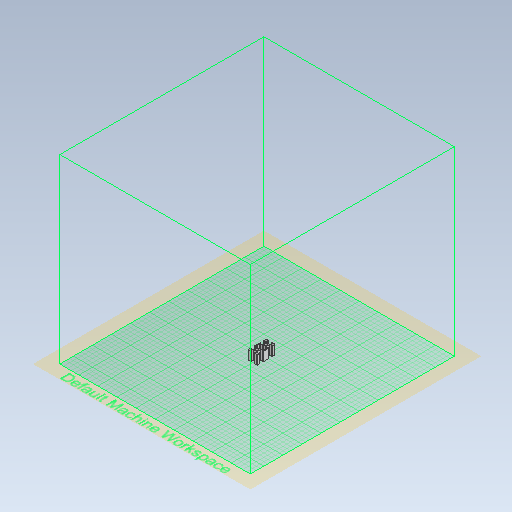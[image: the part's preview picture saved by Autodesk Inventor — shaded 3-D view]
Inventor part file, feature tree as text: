
AUTODESK INVENTOR PART (.ipt)
format: ipt  version: 2020 (Build 240168000, 168)  size: 684,032 bytes
history: native  units: mm
features: fillet x6, extrude x1, sketch x1
ambient origin geometry x8: Origin, YZ Plane, XZ Plane, XY Plane, X Axis, Y Axis, Z Axis, Center Point
bodies: Solid1 (feature_tree)
feature tree (8):
  extrude  "380mm"  Depth=380.0mm TaperAngle=0.0deg
  fillet  "Fillet 0.2mm"  Radius=0.2mm
  fillet  "Fillet 1.5mm"  Radius=1.2mm
  fillet  "Fillet 0.2mm - Extra 1"  Radius=1.5mm
  fillet  "Fillet 0.2mm - Extra 2"  Radius=0.2mm
  fillet  "Fillet 0.2mm - Extra 3"  Radius=0.2mm
  fillet  "Fillet 0.2mm - Extra 4"  Radius=0.2mm
  sketch  "Sketch1"  dims[d1=20.0mm d2=7.2mm d3=0.9mm d4=6.2mm d5=1.8mm d6=10.9mm d8=5.0mm d9=6.1mm d10=380.0mm d11=0.0mm d12=0.2mm d13=1.2mm d14=1.5mm d15=0.2mm d16=0.2mm d17=0.2mm d18=0.2mm d19=1.2mm]
